# Revit family: Drain_Channel_Nero_TileInsert_50mmOutlet
name_source: partatom
category: Plumbing Fixtures
units: mm (PartAtom-declared; Revit-internal decimal feet)

## family parameters
Always vertical = Yes
Cut with Voids When Loaded = Yes
Maintain Annotation Orientation = No
OmniClass Number = 23.31.11.00
OmniClass Title = Faucets
Part Type = Normal
Room Calculation Point = No
Round Connector Dimension = Use Diameter
Shared = No
Work Plane-Based = No

## types (10) — shared parameters
Assembly Code = D2010
CW Connection = Yes
HW Connection = Yes
IfcExportAs = IfcSanitaryTerminal
IfcExportType = NOTDEFINED
Manufacturer = Nero
ManufacturerOverallDepth = 82 mm  [stored 0.269029 ft]
ManufacturerOverallHeight = 76 mm  [stored 0.249344 ft]
ManufacturerURLProductSpecific = https://nerotapware.com.au
ModifiedIssue = 20251105 $
URL = https://nerotapware.com.au
Uniclass2015Code = Pr_65_52_24_24
Uniclass2015Title = Drainage channels with gratings
Uniclass2015Version = Products v1.35
Vent Connection = No
Waste Connection = No
zero-valued in all types: CWFU, Default Elevation, HWFU, WFU

## per-type parameters (varying)
| type | Description | ManufacturerOverallWidth | ManufacturerSpecCode | Material | Model | Type Comments |
| Brushed Bronze (NRFG007HSBZ) | Tile Insert V Channel 1200mm Floor Grate 50mm Outlet With Hole Saw Brushed Bronze | 1200 mm  [stored 3.93701 ft] | NRFG007HSBZ | Metal_Bronze_Nero_Brushed | NRFG007HSBZ | Drain - Channel - 50mm Outlet - Brushed Bronze |
| Brushed Nickel (NRFG007HSBN) | Tile Insert V Channel 1200mm Floor Grate 50mm Outlet With Hole Saw Brushed Nickel | 1200 mm  [stored 3.93701 ft] | NRFG007HSBN | Metal_Nickel_Nero_Brushed | NRFG007HSBN | Drain - Channel - 50mm Outlet - Brushed Nickel |
| Brushed Gold (NRFG007HSBG) | Tile Insert V Channel 1200mm Floor Grate 50mm Outlet With Hole Saw Brushed Gold | 1200 mm  [stored 3.93701 ft] | NRFG007HSBG | Metal_Gold_Nero_Brushed | NRFG007HSBG | Drain - Channel - 50mm Outlet - Brushed Gold |
| Matte Black (NRFG007HSMB) | Tile Insert V Channel 1200mm Floor Grate 50mm Outlet With Hole Saw Matte Black | 1200 mm  [stored 3.93701 ft] | NRFG007HSMB | Metal_MatteBlack_Nero | NRFG007HSMB | Drain - Channel - 50mm Outlet - Matte Black |
| Gunmetal (NRFG007HSGM) | Tile Insert V Channel 1200mm Floor Grate 50mm Outlet With Hole Saw Gun Metal | 1200 mm  [stored 3.93701 ft] | NRFG007HSGM | Metal_GunMetal_Nero | NRFG007HSGM | Drain - Channel - 50mm Outlet - Gunmetal |
| Brushed Bronze (NRFG006HSBZ) | Tile Insert V Channel 600mm Floor Grate 50mm Outlet With Hole Saw | 600 mm  [stored 1.9685 ft] | NRFG006HSBZ | Metal_Bronze_Nero_Brushed | NRFG006HSBZ | Drain - Channel - 50mm Outlet - Brushed Bronze |
| Brushed Nickel (NRFG006HSBN) | Tile Insert V Channel 600mm Floor Grate 50mm Outlet With Hole Saw Brushed Nickel | 600 mm  [stored 1.9685 ft] | NRFG006HSBN | Metal_Nickel_Nero_Brushed | NRFG006HSBN | Drain - Channel - 50mm Outlet - Brushed Nickel |
| Brushed Gold (NRFG006HSBG) | Tile Insert V Channel 600mm Floor Grate 50mm Outlet With Hole Saw Brushed Gold | 600 mm  [stored 1.9685 ft] | NRFG006HSBG | Metal_Gold_Nero_Brushed | NRFG006HSBG | Drain - Channel - 50mm Outlet - Brushed Gold |
| Matte Black (NRFG006HSMB) | Tile Insert V Channel 600mm Floor Grate 50mm Outlet With Hole Saw Matte Black | 600 mm  [stored 1.9685 ft] | NRFG006HSMB | Metal_MatteBlack_Nero | NRFG006HSMB | Drain - Channel - 50mm Outlet - Matte Black |
| Gunmetal (NRFG006HSGM) | Tile Insert V Channel 600mm Floor Grate 50mm Outlet With Hole Saw Gun Metal | 600 mm  [stored 1.9685 ft] | NRFG006HSGM | Metal_GunMetal_Nero | NRFG006HSGM | Drain - Channel - 50mm Outlet - Gunmetal |

note: [stored X ft] marks values corroborated as IEEE doubles in the binary element streams (Revit-internal decimal feet)

## geometry (parser evidence)
native form markers: Sweep x2
no freeform markers — native parametric forms only
